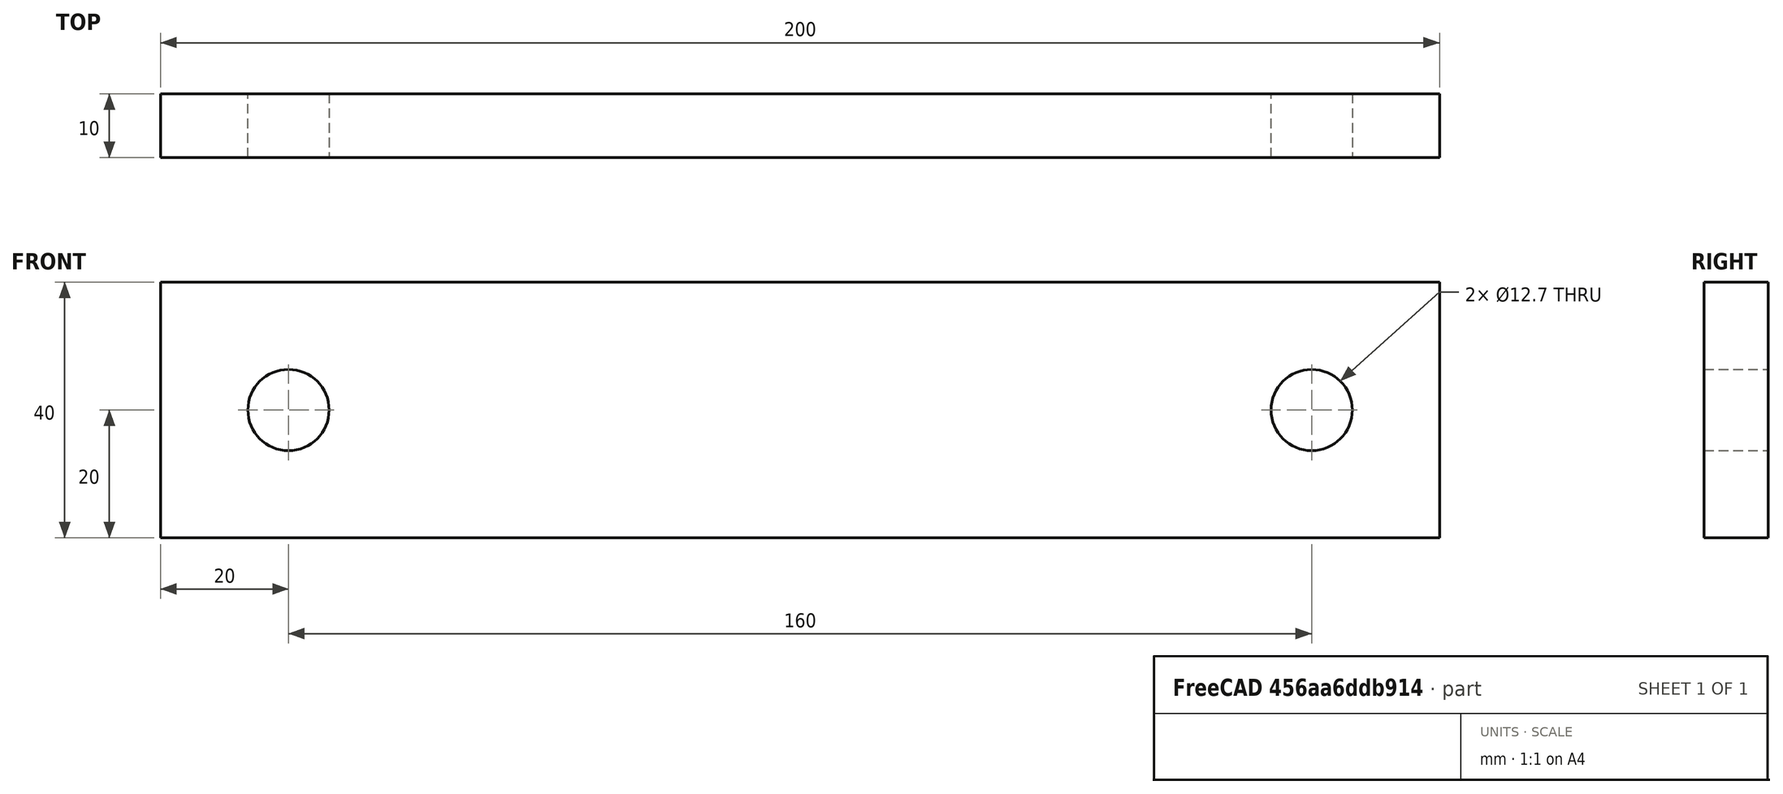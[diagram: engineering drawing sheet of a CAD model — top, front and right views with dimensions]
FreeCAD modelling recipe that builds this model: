
FCSTD DOCUMENT  (FreeCAD 0.18R4 (GitTag))
Label: manivela1
License: All rights reserved
LicenseURL: http://en.wikipedia.org/wiki/All_rights_reserved
objects: Sketcher::SketchObject×1, PartDesign::Pad×1, PartDesign::Body×1
note: 4 computed .brp shape members not serialized (recipe doc carries the construction recipe); baked Part::Feature solids carry a one-line shape summary decoded from their .brp

FEATURE [Sketcher::SketchObject] Sketch
  MapMode = 5
  Placement = pos=(0,0,0) rot=(1,0,0;1.5708rad)
  Support = -> [XZ_Plane]
  sketch-geometry (6):
    g0: LineSegment StartX=0 StartY=0 StartZ=0 EndX=200 EndY=0 EndZ=0
    g1: LineSegment StartX=200 StartY=0 StartZ=0 EndX=200 EndY=40 EndZ=0
    g2: LineSegment StartX=200 StartY=40 StartZ=0 EndX=0 EndY=40 EndZ=0
    g3: LineSegment StartX=0 StartY=40 StartZ=0 EndX=0 EndY=0 EndZ=0
    g4: Circle CenterX=20 CenterY=20 CenterZ=0 NormalX=0 NormalY=0 NormalZ=1 AngleXU=0 Radius=6.35
    g5: Circle CenterX=180 CenterY=20 CenterZ=0 NormalX=0 NormalY=0 NormalZ=1 AngleXU=0 Radius=6.35
  constraints (17):
    c: Coincident(g0,g1)
    c: Coincident(g1,g2)
    c: Coincident(g2,g3)
    c: Coincident(g3,g0)
    c: Horizontal(g0)
    c: Horizontal(g2)
    c: Vertical(g1)
    c: Vertical(g3)
    c: DistanceY(g3,g3) = 40
    c: DistanceX(g0,g0) = 200
    c: Coincident(g0,g-1)
    c: Distance(g5,g1) = 20
    c: Distance(g5,g2) = 20
    c: Distance(g4,g2) = 20
    c: Distance(g4,g3) = 20
    c: Radius(g4) = 6.35
    c: Radius(g5) = 6.35
FEATURE [PartDesign::Pad] Pad
  Length = 10
  Length2 = 100
  Placement = pos=(0,0,0) rot=(1,0,0;1.5708rad)
  Profile = -> Sketch
  Type = 0
FEATURE [PartDesign::Body] Body
  Group = -> [Sketch,Pad]
  Origin = -> Origin
  Tip = -> Pad
